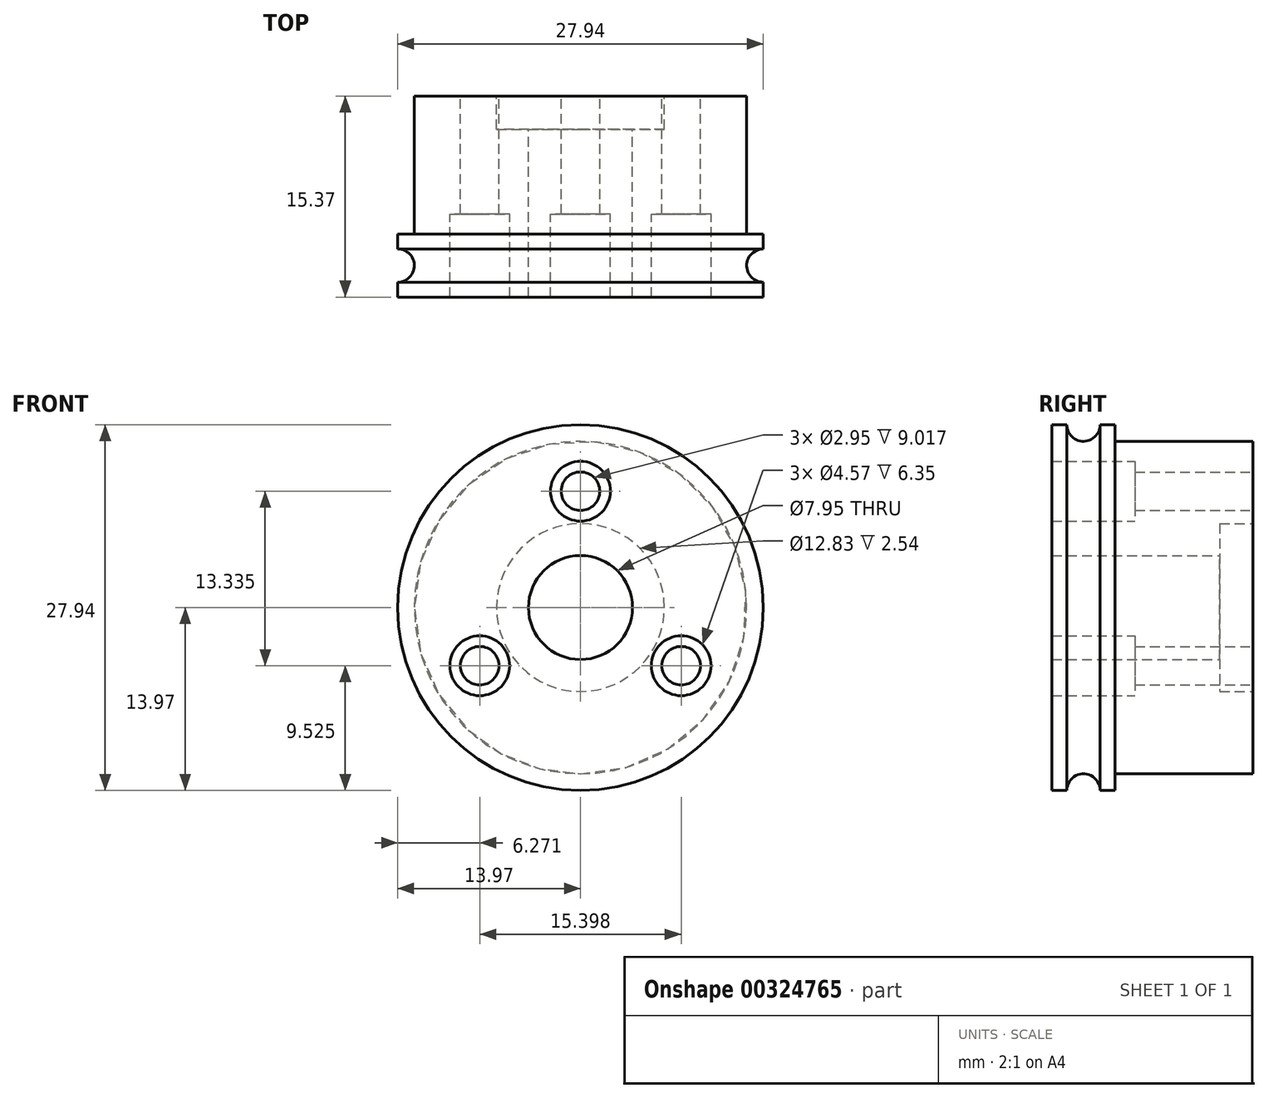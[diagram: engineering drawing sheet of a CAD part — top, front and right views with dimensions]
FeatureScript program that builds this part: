
annotation { "Feature Type Name" : "Feature", "Feature Type Description" : "" }
export const myFeature = defineFeature(function(context is Context, id is Id, definition is map)
    precondition{}
    {
        {
            var Q0;
            Q0=qCreatedBy(makeId("Front.planeOp"),FACE);
            var sketch = newSketch(context, id + "F0", { "sketchPlane" : qUnion([Q0])});
            skCircle(sketch, "E0", {"center": v(0, 0) * mm, "radius": 13.97 * mm});
            skCircle(sketch, "E1", {"center": v(0, 0) * mm, "radius": 3.98 * mm});
            skSolve(sketch);
        }
        {
            var Q0;
            Q0=makeQuery(id+"F0.imprint","IMPRINT",FACE,{"disambiguationData":[TD([[makeQuery(id+"F0.imprint","IMPRINT",EDGE,{"derivedFrom":sQuery(id+"F0.wireOp",EDGE,"E0")}),1.0]])]});
            extrude(context, id + "F1", {"entities" : qUnion([Q0]), "depth" : 15.37 * mm, "offsetDistance" : 25.4 * mm});
        }
        {
            var Q0;
            Q0=makeQuery(id+"F1.opExtrude","CAP_FACE",FACE,{"disambiguationData":[OSD([sQuery(id+"F0.wireOp",EDGE,"E0"),sQuery(id+"F0.wireOp",EDGE,"E1")])],"isStart":false});
            var sketch = newSketch(context, id + "F2", { "sketchPlane" : qUnion([Q0])});
            skPoint(sketch, "E2", {"position": v(0, 8.9) * mm});
            skPoint(sketch, "E3.1.0", {"position": v(-7.7, -4.44) * mm});
            skPoint(sketch, "E3.2.0", {"position": v(7.7, -4.45) * mm});
            skPoint(sketch, "E3.center", {"position": v(0, 0) * mm});
            skSolve(sketch);
        }
        {
            var Q0;
            Q0=sQuery(id+"F2.wireOp",VERTEX,"E2");
            var Q1;
            Q1=sQuery(id+"F2.wireOp",VERTEX,"E3.1.0");
            var Q2;
            Q2=sQuery(id+"F2.wireOp",VERTEX,"E3.2.0");
            var Q3;
            Q3=makeQuery(id+"F1.opExtrude","SWEPT_BODY",BODY,{"disambiguationData":[OSD([sQuery(id+"F0.wireOp",EDGE,"E0"),sQuery(id+"F0.wireOp",EDGE,"E1")])]});
            hole(context, id + "F3", {"style" : HoleStyle.C_BORE, "endStyle" : HoleEndStyle.THROUGH, "holeDiameter" : 2.95 * mm, "cBoreDiameter" : 4.57 * mm, "cBoreDepth" : 6.35 * mm, "majorDiameter" : 6.35 * mm, "tappedDepth" : 12.7 * mm, "tapClearance" : 3, "locations" : qUnion([Q0, Q1, Q2]), "scope" : qUnion([Q3])});
        }
        {
            var Q0;
            Q0=makeQuery(id+"F1.opExtrude","CAP_FACE",FACE,{"disambiguationData":[OSD([sQuery(id+"F0.wireOp",EDGE,"E0"),sQuery(id+"F0.wireOp",EDGE,"E1")])],"isStart":true});
            var sketch = newSketch(context, id + "F4", { "sketchPlane" : qUnion([Q0])});
            skCircle(sketch, "E4", {"center": v(0, 0) * mm, "radius": 6.41 * mm});
            skSolve(sketch);
        }
        {
            var Q0;
            Q0=makeQuery(id+"F4.imprint","IMPRINT",FACE,{"disambiguationData":[TD([[makeQuery(id+"F4.imprint","IMPRINT",EDGE,{"derivedFrom":sQuery(id+"F4.wireOp",EDGE,"E4")}),1.0]])]});
            extrude(context, id + "F5", {"entities" : qUnion([Q0]), "operationType" : NewBodyOperationType.REMOVE, "oppositeDirection" : true, "depth" : 2.54 * mm, "offsetDistance" : 25.4 * mm});
        }
        {
            var Q0;
            Q0=qCreatedBy(makeId("Right.planeOp"),FACE);
            var sketch = newSketch(context, id + "F6", { "sketchPlane" : qUnion([Q0])});
            skCircle(sketch, "E5", {"center": v(-12.95, 13.97) * mm, "radius": 1.27 * mm});
            skSolve(sketch);
        }
        {
            var Q0;
            Q0=makeQuery(id+"F6.imprint","IMPRINT",FACE,{"disambiguationData":[TD([[makeQuery(id+"F6.imprint","IMPRINT",EDGE,{"derivedFrom":sQuery(id+"F6.wireOp",EDGE,"E5")}),1.0]])]});
            var Q1;
            Q1=makeQuery(id+"F1.opExtrude","CAP_EDGE",EDGE,{"disambiguationData":[OSD([sQuery(id+"F0.wireOp",EDGE,"E0")])],"isStart":false});
            sweep(context, id + "F7", {"operationType" : NewBodyOperationType.REMOVE, "profiles" : qUnion([Q0]), "path" : qUnion([Q1])});
        }
        {
            var Q0;
            Q0=makeQuery(id+"F1.opExtrude","CAP_FACE",FACE,{"disambiguationData":[OSD([sQuery(id+"F0.wireOp",EDGE,"E0"),sQuery(id+"F0.wireOp",EDGE,"E1")])],"isStart":true});
            var sketch = newSketch(context, id + "F8", { "sketchPlane" : qUnion([Q0])});
            skCircle(sketch, "E6", {"center": v(0, 0) * mm, "radius": 12.7 * mm});
            skSolve(sketch);
        }
        {
            var Q0;
            Q0=makeQuery(id+"F8.imprint","IMPRINT",FACE,{"disambiguationData":[TD([[makeQuery(id+"F8.imprint","IMPRINT",EDGE,{"derivedFrom":sQuery(id+"F8.wireOp",EDGE,"E6")}),-1.0]])]});
            extrude(context, id + "F9", {"entities" : qUnion([Q0]), "operationType" : NewBodyOperationType.REMOVE, "oppositeDirection" : true, "depth" : 10.54 * mm, "offsetDistance" : 25.4 * mm});
        }
    });
